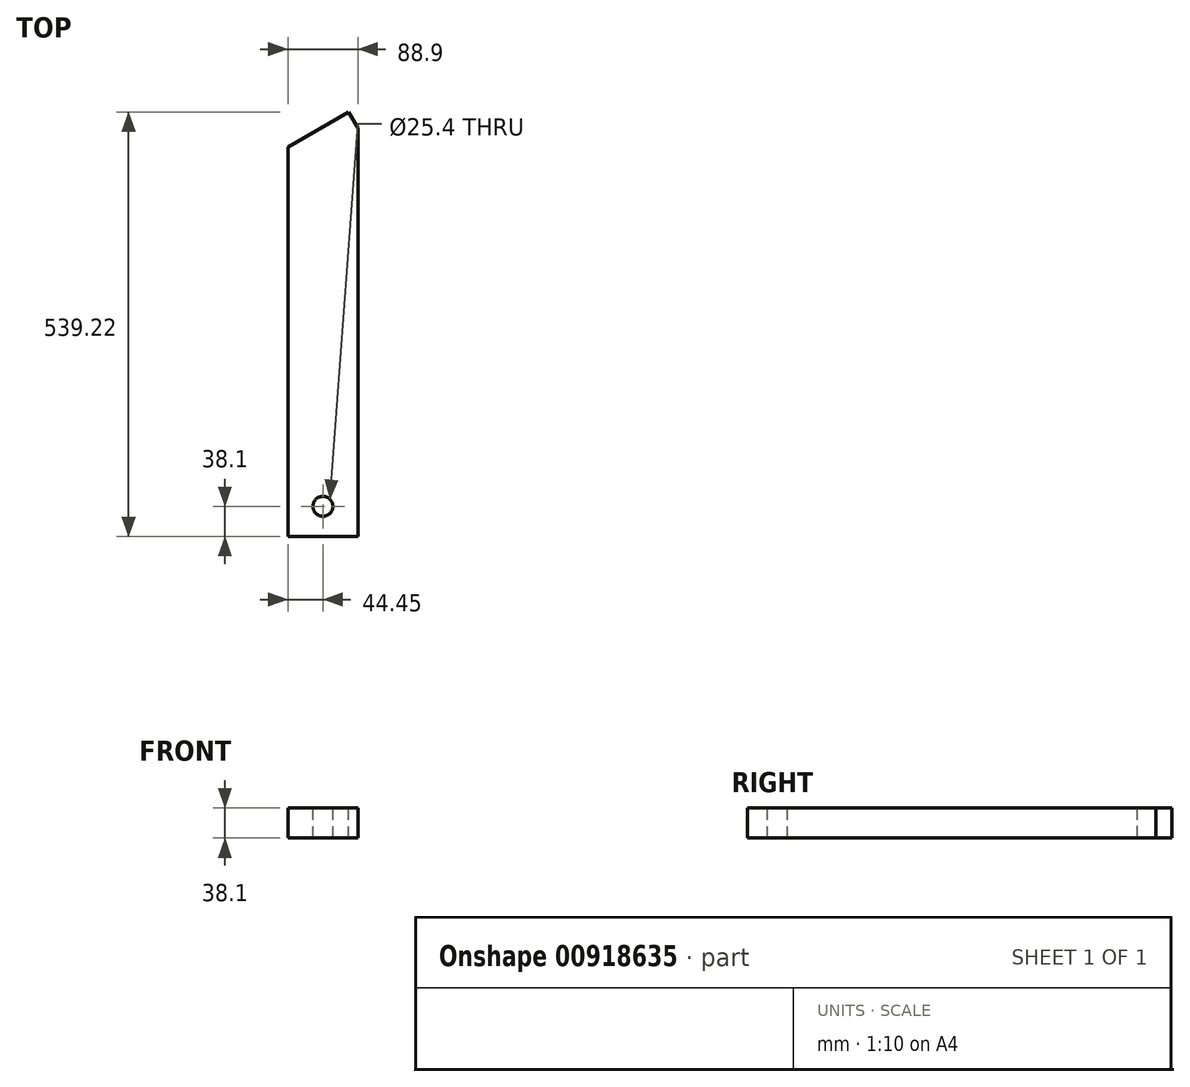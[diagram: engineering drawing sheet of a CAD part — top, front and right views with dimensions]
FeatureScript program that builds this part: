
annotation { "Feature Type Name" : "Feature", "Feature Type Description" : "" }
export const myFeature = defineFeature(function(context is Context, id is Id, definition is map)
    precondition{}
    {
        {
            var Q0;
            Q0=qCreatedBy(makeId("Top.planeOp"),FACE);
            var sketch = newSketch(context, id + "F0", { "sketchPlane" : qUnion([Q0])});
            skLineSegment(sketch, "E0", {"start": v(-88.9, -51.33) * mm, "end": v(0, 0) * mm});
            skLineSegment(sketch, "E1", {"start": v(0, 0) * mm, "end": v(0, -546.1) * mm});
            skLineSegment(sketch, "E2", {"start": v(0, -546.1) * mm, "end": v(-88.9, -546.1) * mm});
            skLineSegment(sketch, "E3", {"start": v(-88.9, -546.1) * mm, "end": v(-88.9, -51.33) * mm});
            skSolve(sketch);
        }
        {
            var Q0;
            Q0=makeQuery(id+"F0.imprint","IMPRINT",FACE,{"disambiguationData":[TD([[makeQuery(id+"F0.imprint","IMPRINT",EDGE,{"derivedFrom":sQuery(id+"F0.wireOp",EDGE,"E0")}),-1.0]])]});
            extrude(context, id + "F1", {"entities" : qUnion([Q0]), "depth" : 38.1 * mm, "offsetDistance" : 25.4 * mm, "symmetric" : true});
        }
        {
            var Q0;
            Q0=makeQuery(id+"F1.opExtrude","CAP_FACE",FACE,{"disambiguationData":[OSD([sQuery(id+"F0.wireOp",EDGE,"E0"),sQuery(id+"F0.wireOp",EDGE,"E1"),sQuery(id+"F0.wireOp",EDGE,"E2"),sQuery(id+"F0.wireOp",EDGE,"E3")])],"isStart":false});
            var sketch = newSketch(context, id + "F2", { "sketchPlane" : qUnion([Q0])});
            skLineSegment(sketch, "E4", {"start": v(0, 0) * mm, "end": v(-11.91, -6.88) * mm});
            skLineSegment(sketch, "E5", {"start": v(-11.91, -6.88) * mm, "end": v(0, -27.5) * mm});
            skLineSegment(sketch, "E6", {"start": v(0, -27.5) * mm, "end": v(0, 0) * mm});
            skSolve(sketch);
        }
        {
            var Q0;
            Q0=makeQuery(id+"F2.imprint","IMPRINT",FACE,{"disambiguationData":[TD([[makeQuery(id+"F2.imprint","IMPRINT",EDGE,{"derivedFrom":sQuery(id+"F2.wireOp",EDGE,"E4")}),-1.0]])]});
            extrude(context, id + "F3", {"entities" : qUnion([Q0]), "operationType" : NewBodyOperationType.REMOVE, "endBound" : BoundingType.THROUGH_ALL, "oppositeDirection" : true, "depth" : 25.4 * mm, "offsetDistance" : 25.4 * mm});
        }
        {
            var Q0;
            Q0=makeQuery(id+"F1.opExtrude","CAP_FACE",FACE,{"disambiguationData":[OSD([sQuery(id+"F0.wireOp",EDGE,"E0"),sQuery(id+"F0.wireOp",EDGE,"E1"),sQuery(id+"F0.wireOp",EDGE,"E2"),sQuery(id+"F0.wireOp",EDGE,"E3")])],"isStart":false});
            var sketch = newSketch(context, id + "F4", { "sketchPlane" : qUnion([Q0])});
            skCircle(sketch, "E7", {"center": v(-44.45, -508) * mm, "radius": 12.7 * mm});
            skLineSegment(sketch, "E8", {"start": v(-44.45, -546.1) * mm, "end": v(-44.45, -508) * mm, "construction": true});
            skSolve(sketch);
        }
        {
            var Q0;
            Q0=makeQuery(id+"F4.imprint","IMPRINT",FACE,{"disambiguationData":[TD([[makeQuery(id+"F4.imprint","IMPRINT",EDGE,{"derivedFrom":sQuery(id+"F4.wireOp",EDGE,"E7")}),1.0]])]});
            extrude(context, id + "F5", {"entities" : qUnion([Q0]), "operationType" : NewBodyOperationType.REMOVE, "endBound" : BoundingType.THROUGH_ALL, "oppositeDirection" : true, "depth" : 25.4 * mm, "offsetDistance" : 25.4 * mm});
        }
    });
